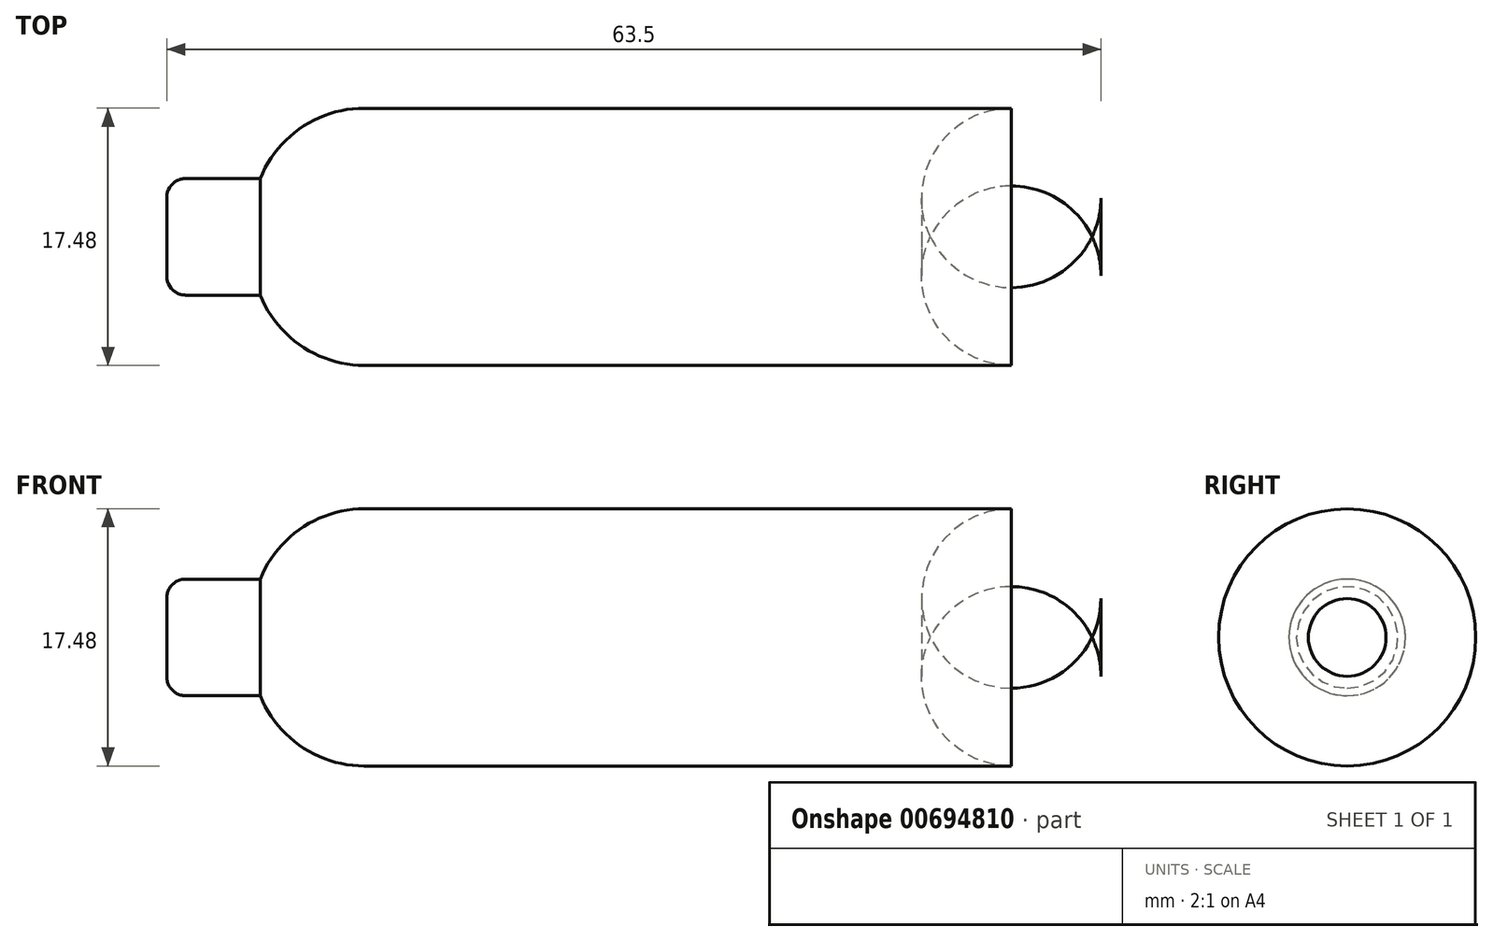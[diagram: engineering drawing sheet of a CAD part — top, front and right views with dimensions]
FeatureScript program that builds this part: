
annotation { "Feature Type Name" : "Feature", "Feature Type Description" : "" }
export const myFeature = defineFeature(function(context is Context, id is Id, definition is map)
    precondition{}
    {
        {
            var Q0;
            Q0=qCreatedBy(makeId("Front.planeOp"),FACE);
            var sketch = newSketch(context, id + "F0", { "sketchPlane" : qUnion([Q0])});
            skLineSegment(sketch, "E0", {"start": v(38.2, 8.74) * mm, "end": v(38.2, 0) * mm});
            skLineSegment(sketch, "E1", {"start": v(38.2, 0) * mm, "end": v(-25.3, 0) * mm});
            skLineSegment(sketch, "E2", {"start": v(-25.3, 0) * mm, "end": v(-25.3, 3.96) * mm});
            skLineSegment(sketch, "E3", {"start": v(-25.3, 3.96) * mm, "end": v(-18.94, 3.96) * mm});
            skLineSegment(sketch, "E4", {"start": v(-18.94, 3.96) * mm, "end": v(-18.94, 8.74) * mm});
            skLineSegment(sketch, "E5", {"start": v(-18.94, 8.74) * mm, "end": v(38.2, 8.74) * mm});
            skSolve(sketch);
        }
        {
            var Q0;
            Q0=makeQuery(id+"F0.imprint","IMPRINT",FACE,{"disambiguationData":[TD([[makeQuery(id+"F0.imprint","IMPRINT",EDGE,{"derivedFrom":sQuery(id+"F0.wireOp",EDGE,"E0")}),-1.0]])]});
            var Q1;
            Q1=sQuery(id+"F0.wireOp",EDGE,"E1");
            revolve(context, id + "F1", {"entities" : qUnion([Q0]), "axis" : qUnion([Q1]), "revolveType" : RevolveType.FULL});
        }
        {
            var Q0;
            Q0=makeQuery(id+"F1.opRevolve","SWEPT_FACE",FACE,{"disambiguationData":[OSD([sQuery(id+"F0.wireOp",EDGE,"E0")])]});
            fillet(context, id + "F2", {"entities" : qUnion([Q0]), "radius" : 6.1 * mm, "tangentPropagation" : true, "allowEdgeOverflow" : false});
        }
        {
            var Q0;
            Q0=makeQuery(id+"F1.opRevolve","SWEPT_EDGE",EDGE,{"disambiguationData":[OSD([sQuery(id+"F0.wireOp",EDGE,"E4"),sQuery(id+"F0.wireOp",EDGE,"E5")])]});
            fillet(context, id + "F3", {"entities" : qUnion([Q0]), "radius" : 7.62 * mm, "tangentPropagation" : true, "allowEdgeOverflow" : false});
        }
        {
            var Q0;
            Q0=makeQuery(id+"F1.opRevolve","SWEPT_FACE",FACE,{"disambiguationData":[OSD([sQuery(id+"F0.wireOp",EDGE,"E2")])]});
            fillet(context, id + "F4", {"entities" : qUnion([Q0]), "radius" : 1.27 * mm, "tangentPropagation" : true, "allowEdgeOverflow" : false});
        }
    });
